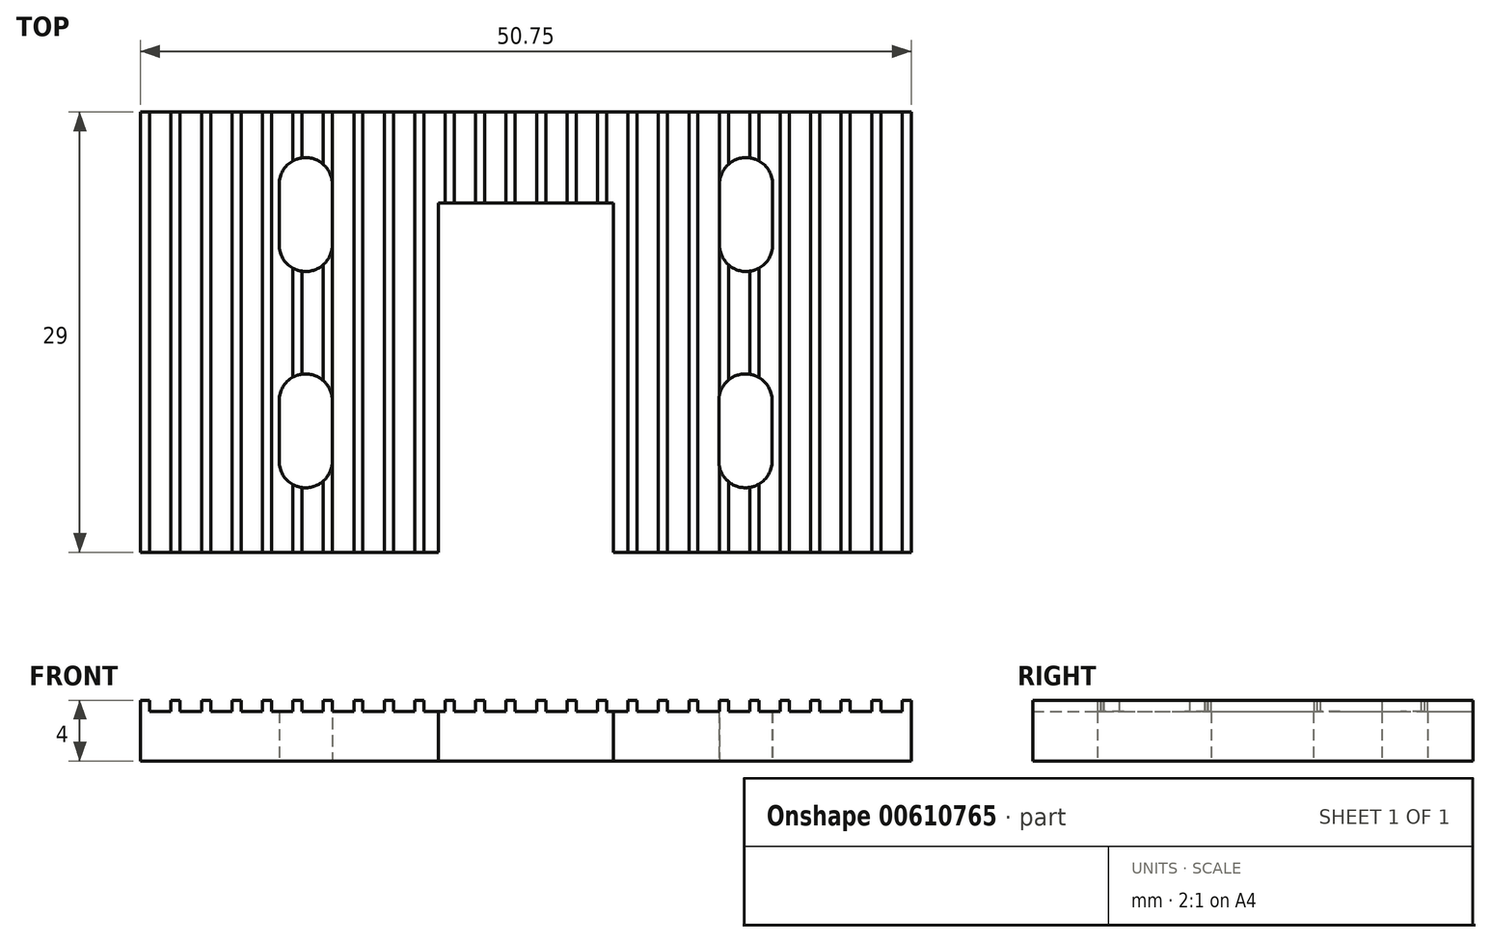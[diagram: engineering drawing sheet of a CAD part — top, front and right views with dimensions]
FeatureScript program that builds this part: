
annotation { "Feature Type Name" : "Feature", "Feature Type Description" : "" }
export const myFeature = defineFeature(function(context is Context, id is Id, definition is map)
    precondition{}
    {
        {
            var Q0;
            Q0=qCreatedBy(makeId("Front.planeOp"),FACE);
            var sketch = newSketch(context, id + "F0", { "sketchPlane" : qUnion([Q0]), "disableImprinting" : false});
            skLineSegment(sketch, "E0", {"start": v(0, 0) * mm, "end": v(0, 4) * mm});
            skLineSegment(sketch, "E1", {"start": v(0, 4) * mm, "end": v(0.6, 4) * mm});
            skLineSegment(sketch, "E2", {"start": v(0.6, 4) * mm, "end": v(0.6, 3.25) * mm});
            skLineSegment(sketch, "E3", {"start": v(0.6, 3.25) * mm, "end": v(2, 3.25) * mm});
            skLineSegment(sketch, "E4", {"start": v(2, 3.25) * mm, "end": v(2, 4) * mm});
            skLineSegment(sketch, "E5", {"start": v(2, 4) * mm, "end": v(2.6, 4) * mm});
            skLineSegment(sketch, "E6", {"start": v(2.6, 4) * mm, "end": v(2.6, 3.25) * mm});
            skLineSegment(sketch, "E7", {"start": v(2.6, 3.25) * mm, "end": v(4.01, 3.25) * mm});
            skLineSegment(sketch, "E8", {"start": v(4.01, 3.25) * mm, "end": v(4.01, 4) * mm});
            skLineSegment(sketch, "E9", {"start": v(4.01, 4) * mm, "end": v(4.61, 4) * mm});
            skLineSegment(sketch, "E10", {"start": v(4.61, 4) * mm, "end": v(4.61, 3.25) * mm});
            skLineSegment(sketch, "E11.1.0.0", {"start": v(6.02, 4) * mm, "end": v(6.62, 4) * mm});
            skLineSegment(sketch, "E11.1.0.1", {"start": v(6.02, 3.25) * mm, "end": v(6.02, 4) * mm});
            skLineSegment(sketch, "E11.1.0.2", {"start": v(6.62, 4) * mm, "end": v(6.62, 3.25) * mm});
            skLineSegment(sketch, "E11.2.0.0", {"start": v(8.02, 4) * mm, "end": v(8.62, 4) * mm});
            skLineSegment(sketch, "E11.2.0.1", {"start": v(8.02, 3.25) * mm, "end": v(8.02, 4) * mm});
            skLineSegment(sketch, "E11.2.0.2", {"start": v(8.62, 4) * mm, "end": v(8.62, 3.25) * mm});
            skLineSegment(sketch, "E11.3.0.0", {"start": v(10.03, 4) * mm, "end": v(10.63, 4) * mm});
            skLineSegment(sketch, "E11.3.0.1", {"start": v(10.03, 3.25) * mm, "end": v(10.03, 4) * mm});
            skLineSegment(sketch, "E11.3.0.2", {"start": v(10.63, 4) * mm, "end": v(10.63, 3.25) * mm});
            skLineSegment(sketch, "E11.4.0.0", {"start": v(12.04, 4) * mm, "end": v(12.64, 4) * mm});
            skLineSegment(sketch, "E11.4.0.1", {"start": v(12.04, 3.25) * mm, "end": v(12.04, 4) * mm});
            skLineSegment(sketch, "E11.4.0.2", {"start": v(12.64, 4) * mm, "end": v(12.64, 3.25) * mm});
            skLineSegment(sketch, "E11.5.0.0", {"start": v(14.04, 4) * mm, "end": v(14.64, 4) * mm});
            skLineSegment(sketch, "E11.5.0.1", {"start": v(14.04, 3.25) * mm, "end": v(14.04, 4) * mm});
            skLineSegment(sketch, "E11.5.0.2", {"start": v(14.64, 4) * mm, "end": v(14.64, 3.25) * mm});
            skLineSegment(sketch, "E11.6.0.0", {"start": v(16.05, 4) * mm, "end": v(16.65, 4) * mm});
            skLineSegment(sketch, "E11.6.0.1", {"start": v(16.05, 3.25) * mm, "end": v(16.05, 4) * mm});
            skLineSegment(sketch, "E11.6.0.2", {"start": v(16.65, 4) * mm, "end": v(16.65, 3.25) * mm});
            skLineSegment(sketch, "E11.7.0.0", {"start": v(18.05, 4) * mm, "end": v(18.65, 4) * mm});
            skLineSegment(sketch, "E11.7.0.1", {"start": v(18.05, 3.25) * mm, "end": v(18.05, 4) * mm});
            skLineSegment(sketch, "E11.7.0.2", {"start": v(18.65, 4) * mm, "end": v(18.65, 3.25) * mm});
            skLineSegment(sketch, "E11.8.0.0", {"start": v(20.06, 4) * mm, "end": v(20.66, 4) * mm});
            skLineSegment(sketch, "E11.8.0.1", {"start": v(20.06, 3.25) * mm, "end": v(20.06, 4) * mm});
            skLineSegment(sketch, "E11.8.0.2", {"start": v(20.66, 4) * mm, "end": v(20.66, 3.25) * mm});
            skLineSegment(sketch, "E11.9.0.0", {"start": v(22.07, 4) * mm, "end": v(22.67, 4) * mm});
            skLineSegment(sketch, "E11.9.0.1", {"start": v(22.07, 3.25) * mm, "end": v(22.07, 4) * mm});
            skLineSegment(sketch, "E11.9.0.2", {"start": v(22.67, 4) * mm, "end": v(22.67, 3.25) * mm});
            skLineSegment(sketch, "E11.10.0.0", {"start": v(24.07, 4) * mm, "end": v(24.67, 4) * mm});
            skLineSegment(sketch, "E11.10.0.1", {"start": v(24.07, 3.25) * mm, "end": v(24.07, 4) * mm});
            skLineSegment(sketch, "E11.10.0.2", {"start": v(24.67, 4) * mm, "end": v(24.67, 3.25) * mm});
            skLineSegment(sketch, "E11.11.0.0", {"start": v(26.08, 4) * mm, "end": v(26.68, 4) * mm});
            skLineSegment(sketch, "E11.11.0.1", {"start": v(26.08, 3.25) * mm, "end": v(26.08, 4) * mm});
            skLineSegment(sketch, "E11.11.0.2", {"start": v(26.68, 4) * mm, "end": v(26.68, 3.25) * mm});
            skLineSegment(sketch, "E11.12.0.0", {"start": v(28.08, 4) * mm, "end": v(28.68, 4) * mm});
            skLineSegment(sketch, "E11.12.0.1", {"start": v(28.08, 3.25) * mm, "end": v(28.08, 4) * mm});
            skLineSegment(sketch, "E11.12.0.2", {"start": v(28.68, 4) * mm, "end": v(28.68, 3.25) * mm});
            skLineSegment(sketch, "E11.13.0.0", {"start": v(30.1, 4) * mm, "end": v(30.7, 4) * mm});
            skLineSegment(sketch, "E11.13.0.1", {"start": v(30.1, 3.25) * mm, "end": v(30.1, 4) * mm});
            skLineSegment(sketch, "E11.13.0.2", {"start": v(30.7, 4) * mm, "end": v(30.7, 3.25) * mm});
            skLineSegment(sketch, "E11.14.0.0", {"start": v(32.1, 4) * mm, "end": v(32.7, 4) * mm});
            skLineSegment(sketch, "E11.14.0.1", {"start": v(32.1, 3.25) * mm, "end": v(32.1, 4) * mm});
            skLineSegment(sketch, "E11.14.0.2", {"start": v(32.7, 4) * mm, "end": v(32.7, 3.25) * mm});
            skLineSegment(sketch, "E11.15.0.0", {"start": v(34.1, 4) * mm, "end": v(34.7, 4) * mm});
            skLineSegment(sketch, "E11.15.0.1", {"start": v(34.1, 3.25) * mm, "end": v(34.1, 4) * mm});
            skLineSegment(sketch, "E11.15.0.2", {"start": v(34.7, 4) * mm, "end": v(34.7, 3.25) * mm});
            skLineSegment(sketch, "E11.16.0.0", {"start": v(36.1, 4) * mm, "end": v(36.7, 4) * mm});
            skLineSegment(sketch, "E11.16.0.1", {"start": v(36.1, 3.25) * mm, "end": v(36.1, 4) * mm});
            skLineSegment(sketch, "E11.16.0.2", {"start": v(36.7, 4) * mm, "end": v(36.7, 3.25) * mm});
            skLineSegment(sketch, "E11.17.0.0", {"start": v(38.11, 4) * mm, "end": v(38.71, 4) * mm});
            skLineSegment(sketch, "E11.17.0.1", {"start": v(38.11, 3.25) * mm, "end": v(38.11, 4) * mm});
            skLineSegment(sketch, "E11.17.0.2", {"start": v(38.71, 4) * mm, "end": v(38.71, 3.25) * mm});
            skLineSegment(sketch, "E11.18.0.0", {"start": v(40.12, 4) * mm, "end": v(40.72, 4) * mm});
            skLineSegment(sketch, "E11.18.0.1", {"start": v(40.12, 3.25) * mm, "end": v(40.12, 4) * mm});
            skLineSegment(sketch, "E11.18.0.2", {"start": v(40.72, 4) * mm, "end": v(40.72, 3.25) * mm});
            skLineSegment(sketch, "E11.19.0.0", {"start": v(42.13, 4) * mm, "end": v(42.73, 4) * mm});
            skLineSegment(sketch, "E11.19.0.1", {"start": v(42.13, 3.25) * mm, "end": v(42.13, 4) * mm});
            skLineSegment(sketch, "E11.19.0.2", {"start": v(42.73, 4) * mm, "end": v(42.73, 3.25) * mm});
            skLineSegment(sketch, "E11.20.0.0", {"start": v(44.13, 4) * mm, "end": v(44.73, 4) * mm});
            skLineSegment(sketch, "E11.20.0.1", {"start": v(44.13, 3.25) * mm, "end": v(44.13, 4) * mm});
            skLineSegment(sketch, "E11.20.0.2", {"start": v(44.73, 4) * mm, "end": v(44.73, 3.25) * mm});
            skLineSegment(sketch, "E11.21.0.0", {"start": v(46.14, 4) * mm, "end": v(46.74, 4) * mm});
            skLineSegment(sketch, "E11.21.0.1", {"start": v(46.14, 3.25) * mm, "end": v(46.14, 4) * mm});
            skLineSegment(sketch, "E11.21.0.2", {"start": v(46.74, 4) * mm, "end": v(46.74, 3.25) * mm});
            skLineSegment(sketch, "E12", {"start": v(6.62, 3.25) * mm, "end": v(8.02, 3.25) * mm});
            skLineSegment(sketch, "E13", {"start": v(8.62, 3.25) * mm, "end": v(10.03, 3.25) * mm});
            skLineSegment(sketch, "E14", {"start": v(10.63, 3.25) * mm, "end": v(12.04, 3.25) * mm});
            skLineSegment(sketch, "E15", {"start": v(12.64, 3.25) * mm, "end": v(14.04, 3.25) * mm});
            skLineSegment(sketch, "E16", {"start": v(14.64, 3.25) * mm, "end": v(16.05, 3.25) * mm});
            skLineSegment(sketch, "E17", {"start": v(16.65, 3.25) * mm, "end": v(18.05, 3.25) * mm});
            skLineSegment(sketch, "E18", {"start": v(18.65, 3.25) * mm, "end": v(20.06, 3.25) * mm});
            skLineSegment(sketch, "E19", {"start": v(20.66, 3.25) * mm, "end": v(22.07, 3.25) * mm});
            skLineSegment(sketch, "E20", {"start": v(22.67, 3.25) * mm, "end": v(24.07, 3.25) * mm});
            skLineSegment(sketch, "E21", {"start": v(24.67, 3.25) * mm, "end": v(26.08, 3.25) * mm});
            skLineSegment(sketch, "E22", {"start": v(26.68, 3.25) * mm, "end": v(28.08, 3.25) * mm});
            skLineSegment(sketch, "E23", {"start": v(28.68, 3.25) * mm, "end": v(30.1, 3.25) * mm});
            skLineSegment(sketch, "E24", {"start": v(30.7, 3.25) * mm, "end": v(32.1, 3.25) * mm});
            skLineSegment(sketch, "E25", {"start": v(32.7, 3.25) * mm, "end": v(34.1, 3.25) * mm});
            skLineSegment(sketch, "E26", {"start": v(34.7, 3.25) * mm, "end": v(36.1, 3.25) * mm});
            skLineSegment(sketch, "E27", {"start": v(36.7, 3.25) * mm, "end": v(38.11, 3.25) * mm});
            skLineSegment(sketch, "E28", {"start": v(38.71, 3.25) * mm, "end": v(40.12, 3.25) * mm});
            skLineSegment(sketch, "E29", {"start": v(40.72, 3.25) * mm, "end": v(42.13, 3.25) * mm});
            skLineSegment(sketch, "E30", {"start": v(42.73, 3.25) * mm, "end": v(44.13, 3.25) * mm});
            skLineSegment(sketch, "E31", {"start": v(44.73, 3.25) * mm, "end": v(46.14, 3.25) * mm});
            skLineSegment(sketch, "E32", {"start": v(50.75, 0) * mm, "end": v(0, 0) * mm});
            skLineSegment(sketch, "E33.0.22.0", {"start": v(48.14, 4) * mm, "end": v(48.74, 4) * mm});
            skLineSegment(sketch, "E33.3.22.0", {"start": v(48.14, 3.25) * mm, "end": v(48.14, 4) * mm});
            skLineSegment(sketch, "E33.6.22.0", {"start": v(48.74, 4) * mm, "end": v(48.74, 3.25) * mm});
            skLineSegment(sketch, "E33.0.23.0", {"start": v(50.15, 4) * mm, "end": v(50.75, 4) * mm});
            skLineSegment(sketch, "E33.3.23.0", {"start": v(50.15, 3.25) * mm, "end": v(50.15, 4) * mm});
            skLineSegment(sketch, "E33.6.23.0", {"start": v(50.75, 4) * mm, "end": v(50.75, 3.25) * mm});
            skLineSegment(sketch, "E34", {"start": v(46.74, 3.25) * mm, "end": v(48.14, 3.25) * mm});
            skLineSegment(sketch, "E35", {"start": v(48.74, 3.25) * mm, "end": v(50.15, 3.25) * mm});
            skLineSegment(sketch, "E36", {"start": v(4.61, 3.25) * mm, "end": v(6.02, 3.25) * mm});
            skLineSegment(sketch, "E37", {"start": v(8.97, 13.53) * mm, "end": v(13.97, 13.53) * mm});
            skLineSegment(sketch, "E38", {"start": v(13.97, 13.53) * mm, "end": v(13.97, 13.47) * mm});
            skLineSegment(sketch, "E39", {"start": v(13.97, 13.47) * mm, "end": v(13.97, 8.47) * mm});
            skLineSegment(sketch, "E40", {"start": v(13.97, 8.47) * mm, "end": v(18.97, 8.47) * mm});
            skLineSegment(sketch, "E41", {"start": v(18.97, 8.47) * mm, "end": v(18.97, 13.47) * mm});
            skLineSegment(sketch, "E42", {"start": v(18.97, 13.47) * mm, "end": v(23.97, 13.47) * mm});
            skLineSegment(sketch, "E43", {"start": v(6.32, 4) * mm, "end": v(6.32, 5.33) * mm});
            skLineSegment(sketch, "E44", {"start": v(8.32, 4) * mm, "end": v(8.32, 5.33) * mm});
            skLineSegment(sketch, "E45", {"start": v(8.32, 5.33) * mm, "end": v(6.32, 5.33) * mm});
            skLineSegment(sketch, "E46", {"start": v(50.75, 3.25) * mm, "end": v(50.75, 0) * mm});
            skSolve(sketch);
        }
        {
            var Q0;
            Q0=makeQuery(id+"F0.imprint","IMPRINT",FACE,{"disambiguationData":[TD([[makeQuery(id+"F0.imprint","IMPRINT",EDGE,{"derivedFrom":sQuery(id+"F0.wireOp",EDGE,"E0")}),-1.0]])]});
            extrude(context, id + "F1", {"entities" : qUnion([Q0]), "depth" : 29 * mm, "offsetDistance" : 25 * mm});
        }
        {
            var Q0;
            Q0=makeQuery(id+"F1.opExtrude","SWEPT_FACE",FACE,{"disambiguationData":[OSD([sQuery(id+"F0.wireOp",EDGE,"E32")])]});
            var sketch = newSketch(context, id + "F2", { "sketchPlane" : qUnion([Q0])});
            skLineSegment(sketch, "E47", {"start": v(25.37, 29) * mm, "end": v(25.37, 6) * mm});
            skLineSegment(sketch, "E48", {"start": v(19.62, 29) * mm, "end": v(19.62, 6) * mm});
            skLineSegment(sketch, "E49", {"start": v(19.62, 6) * mm, "end": v(25.37, 6) * mm});
            skLineSegment(sketch, "E50", {"start": v(25.37, 6) * mm, "end": v(31.12, 6) * mm});
            skLineSegment(sketch, "E51", {"start": v(31.12, 6) * mm, "end": v(31.12, 29) * mm});
            skPoint(sketch, "E52.orphan", {"position": v(25.37, 0) * mm});
            skLineSegment(sketch, "E53.bottom", {"start": v(9.12, 23) * mm, "end": v(12.62, 23) * mm});
            skLineSegment(sketch, "E53.top", {"start": v(9.12, 19) * mm, "end": v(12.62, 19) * mm});
            skLineSegment(sketch, "E53.left", {"start": v(9.12, 23) * mm, "end": v(9.12, 19) * mm});
            skLineSegment(sketch, "E53.right", {"start": v(12.62, 23) * mm, "end": v(12.62, 19) * mm});
            skLineSegment(sketch, "E54.bottom", {"start": v(9.12, 8.75) * mm, "end": v(12.62, 8.75) * mm});
            skLineSegment(sketch, "E54.top", {"start": v(9.12, 4.75) * mm, "end": v(12.62, 4.75) * mm});
            skLineSegment(sketch, "E54.left", {"start": v(9.12, 8.75) * mm, "end": v(9.12, 4.75) * mm});
            skLineSegment(sketch, "E54.right", {"start": v(12.62, 8.75) * mm, "end": v(12.62, 4.75) * mm});
            skLineSegment(sketch, "E55.bottom", {"start": v(38.08, 23) * mm, "end": v(41.58, 23) * mm});
            skLineSegment(sketch, "E55.top", {"start": v(38.08, 19) * mm, "end": v(41.58, 19) * mm});
            skLineSegment(sketch, "E55.left", {"start": v(38.08, 23) * mm, "end": v(38.08, 19) * mm});
            skLineSegment(sketch, "E55.right", {"start": v(41.58, 23) * mm, "end": v(41.58, 19) * mm});
            skLineSegment(sketch, "E56.bottom", {"start": v(38.12, 8.75) * mm, "end": v(41.62, 8.75) * mm});
            skLineSegment(sketch, "E56.top", {"start": v(38.12, 4.75) * mm, "end": v(41.62, 4.75) * mm});
            skLineSegment(sketch, "E56.left", {"start": v(38.12, 8.75) * mm, "end": v(38.12, 4.75) * mm});
            skLineSegment(sketch, "E56.right", {"start": v(41.62, 8.75) * mm, "end": v(41.62, 4.75) * mm});
            skArc(sketch, "E57", {"start": v(9.12, 23) * mm, "mid": v(10.87, 24.75) * mm, "end": v(12.62, 23) * mm});
            skArc(sketch, "E58", {"start": v(9.12, 19) * mm, "mid": v(10.87, 17.25) * mm, "end": v(12.62, 19) * mm});
            skArc(sketch, "E59", {"start": v(9.12, 8.75) * mm, "mid": v(10.87, 10.5) * mm, "end": v(12.62, 8.75) * mm});
            skArc(sketch, "E60", {"start": v(9.12, 4.75) * mm, "mid": v(10.87, 3) * mm, "end": v(12.62, 4.75) * mm});
            skLineSegment(sketch, "E61", {"start": v(38.08, 23) * mm, "end": v(38.08, 23) * mm});
            skArc(sketch, "E62", {"start": v(41.58, 19) * mm, "mid": v(39.83, 17.25) * mm, "end": v(38.08, 19) * mm});
            skPoint(sketch, "E62.startSnap0", {"position": v(39.83, 19) * mm});
            skArc(sketch, "E63", {"start": v(38.12, 8.75) * mm, "mid": v(39.87, 10.5) * mm, "end": v(41.62, 8.75) * mm});
            skArc(sketch, "E64", {"start": v(41.62, 4.75) * mm, "mid": v(39.87, 3) * mm, "end": v(38.12, 4.75) * mm});
            skArc(sketch, "E65", {"start": v(38.08, 23) * mm, "mid": v(39.83, 24.75) * mm, "end": v(41.58, 23) * mm});
            skSolve(sketch);
        }
        {
            var Q0;
            {var subQ0=sQuery(id+"F2.wireOp",EDGE,"E47");Q0=makeQuery(id+"F2.imprint","IMPRINT",FACE,{"disambiguationData":[TD([[makeQuery(id+"F2.imprint","IMPRINT",EDGE,{"derivedFrom":subQ0}),-1.0]])]});}
            var Q1;
            {var subQ0=sQuery(id+"F2.wireOp",EDGE,"E47");Q1=makeQuery(id+"F2.imprint","IMPRINT",FACE,{"disambiguationData":[TD([[makeQuery(id+"F2.imprint","IMPRINT",EDGE,{"derivedFrom":subQ0}),1.0]])]});}
            extrude(context, id + "F3", {"entities" : qUnion([Q0, Q1]), "operationType" : NewBodyOperationType.REMOVE, "endBound" : BoundingType.UP_TO_NEXT, "oppositeDirection" : true, "depth" : 25 * mm, "offsetDistance" : 25 * mm});
        }
        {
            var Q0;
            Q0=qSketchRegion(id+"F2",true);
            extrude(context, id + "F4", {"entities" : qUnion([Q0]), "operationType" : NewBodyOperationType.REMOVE, "endBound" : BoundingType.UP_TO_NEXT, "oppositeDirection" : true, "depth" : 25 * mm, "offsetDistance" : 25 * mm});
        }
    });
